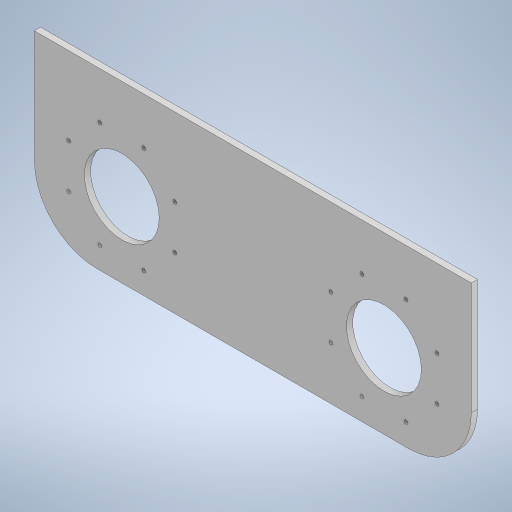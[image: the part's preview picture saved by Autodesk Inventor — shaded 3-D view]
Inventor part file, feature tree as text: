
AUTODESK INVENTOR PART (.ipt)
format: ipt  version: 2024.3 (Build 283343000, 343)  size: 256,512 bytes
history: native  units: mm
features: other x1, extrude x1, fillet x1, sketch x1
ambient origin geometry x8: Origin, YZ Plane, XZ Plane, XY Plane, X Axis, Y Axis, Z Axis, Center Point
bodies: Body1 (feature_tree)
feature tree (4):
  other  "ソリッド1"
  extrude  "押し出し1"  Depth=350.0mm
  fillet  "フィレット2"  Radius=140.0mm
  sketch  "スケッチ1"
